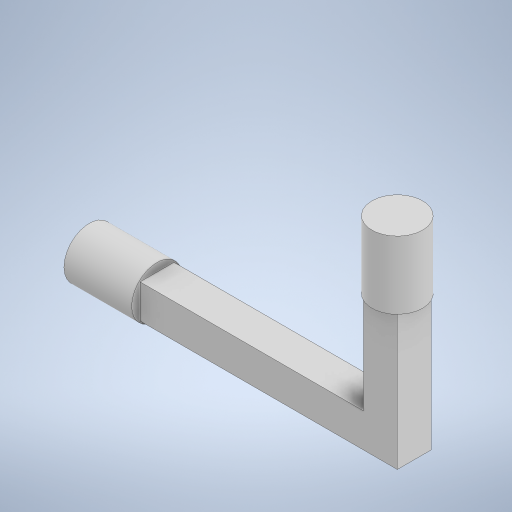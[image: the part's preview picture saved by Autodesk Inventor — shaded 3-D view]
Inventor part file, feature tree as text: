
AUTODESK INVENTOR PART (.ipt)
format: ipt  version: 2024.3 (Build 283343000, 343)  size: 250,368 bytes
history: native  units: mm
features: extrude x3, sketch x3, other x1
ambient origin geometry x8: Origin, YZ Plane, XZ Plane, XY Plane, X Axis, Y Axis, Z Axis, Center Point
bodies: Body1 (feature_tree)
feature tree (7):
  other  "ソリッド1"
  extrude  "押し出し1"  Depth=10.0mm
  extrude  "押し出し2"  Depth=10.0mm
  extrude  "押し出し3"  Depth=60.0mm
  sketch  "スケッチ1"
  sketch  "スケッチ2"
  sketch  "スケッチ3"
